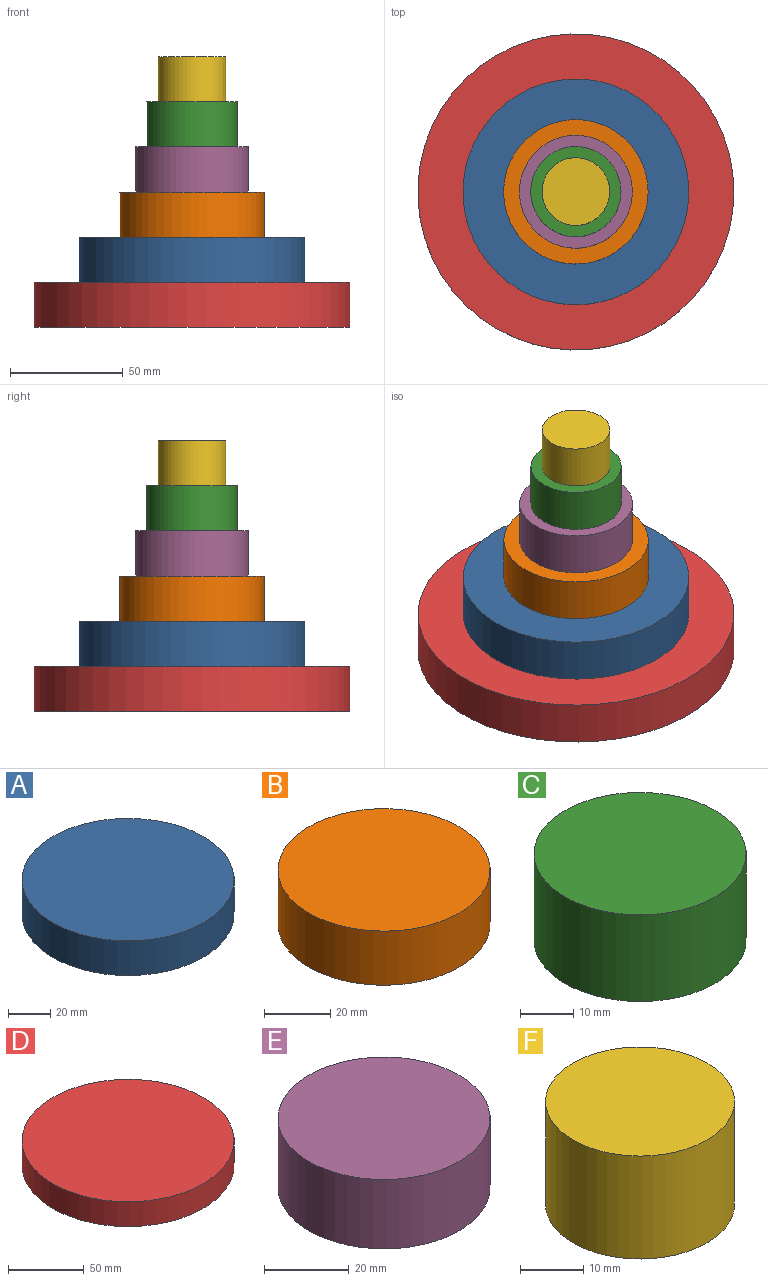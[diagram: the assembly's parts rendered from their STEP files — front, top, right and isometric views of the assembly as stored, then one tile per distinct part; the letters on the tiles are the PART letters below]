
ASSEMBLY  parts=6 mates=5
PART A: 3 faces, bbox 100x100x20 mm
  f0: cylinder r=50mm len=100mm, axis (0,0,-1), area 6283.2mm2, adj f1,f2
  f1: plane 100x100mm, normal (0,0,1), area 7854mm2, adj f0
  f2: plane 100x100mm, normal (0,0,-1), area 7854mm2, adj f0
PART B: 3 faces, bbox 64x64x20 mm
  f0: cylinder r=32mm len=64mm, axis (0,0,-1), area 4021.2mm2, adj f1,f2
  f1: plane 64x64mm, normal (0,0,1), area 3217mm2, adj f0
  f2: plane 64x64mm, normal (0,0,-1), area 3217mm2, adj f0
PART C: 3 faces, bbox 40x40x20 mm
  f0: cylinder r=20mm len=40mm, axis (0,0,-1), area 2513.3mm2, adj f1,f2
  f1: plane 40x40mm, normal (0,0,1), area 1256.6mm2, adj f0
  f2: plane 40x40mm, normal (0,0,-1), area 1256.6mm2, adj f0
PART D: 3 faces, bbox 140x140x20 mm
  f0: cylinder r=70mm len=140mm, axis (0,0,-1), area 8796.5mm2, adj f1,f2
  f1: plane 140x140mm, normal (0,0,1), area 15393.8mm2, adj f0
  f2: plane 140x140mm, normal (0,0,-1), area 15393.8mm2, adj f0
PART E: 3 faces, bbox 50x50x20 mm
  f0: cylinder r=25mm len=50mm, axis (0,0,-1), area 3141.6mm2, adj f1,f2
  f1: plane 50x50mm, normal (0,0,1), area 1963.5mm2, adj f0
  f2: plane 50x50mm, normal (0,0,-1), area 1963.5mm2, adj f0
PART F: 3 faces, bbox 30x30x20 mm
  f0: cylinder r=15mm len=30mm, axis (0,0,-1), area 1885mm2, adj f1,f2
  f1: plane 30x30mm, normal (0,0,1), area 706.9mm2, adj f0
  f2: plane 30x30mm, normal (0,0,-1), area 706.9mm2, adj f0
PLACE A rot(axis=(1,0,0),180deg) t=(-203.06,-8.91,-51.94)mm
PLACE B rot(axis=(1,0,0),180deg) t=(-98.23,-8.91,-31.94)mm
PLACE C rot(axis=(1,0,0),180deg) t=(34.99,-8.91,8.06)mm
PLACE D t=(-346.42,-8.91,-91.94)mm fixed
PLACE E rot(axis=(1,0,0),180deg) t=(-26.53,-8.91,-11.94)mm
PLACE F rot(axis=(1,0,0),180deg) t=(79.19,-8.91,28.06)mm
MATE cylindrical E.f0 <-> B.f0  axis (0,0,-1) through (79.19,-8.91,-31.94)mm
MATE cylindrical F.f0 <-> C.f0  axis (0,0,1) through (79.19,-8.91,8.06)mm
MATE cylindrical C.f0 <-> E.f0  axis (0,0,-1) through (79.19,-8.91,-11.94)mm
MATE cylindrical D.f0 <-> A.f0  axis (0,0,1) through (79.19,-8.91,-71.94)mm
MATE slider A.f0 <-> B.f0  axis (0,0,1) through (79.19,-8.91,-51.94)mm
